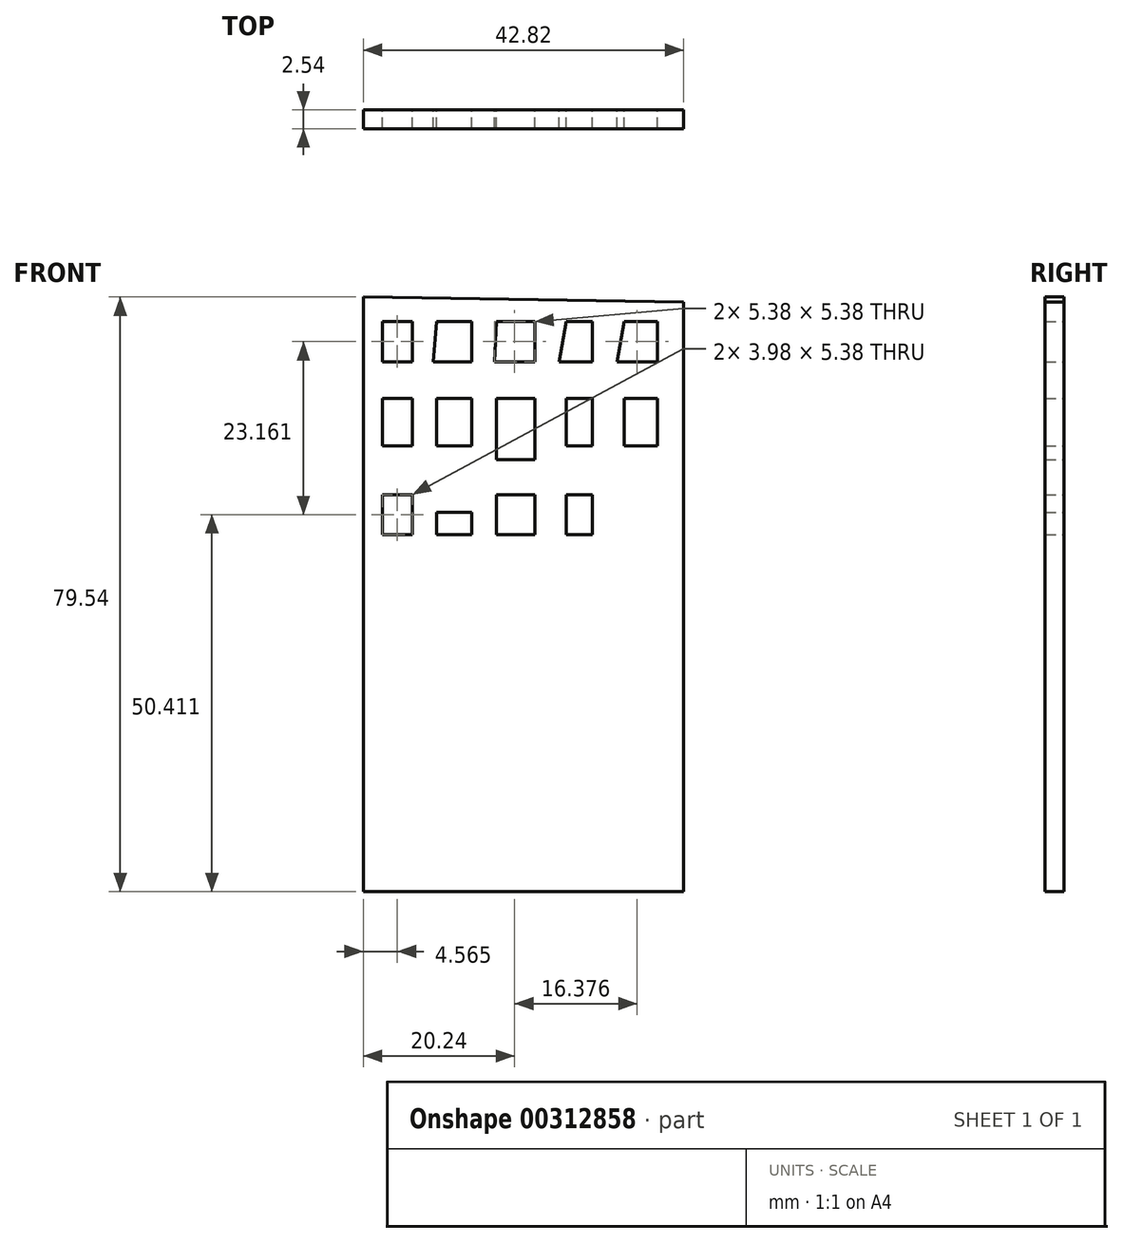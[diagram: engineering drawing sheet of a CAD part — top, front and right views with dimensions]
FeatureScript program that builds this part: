
annotation { "Feature Type Name" : "Feature", "Feature Type Description" : "" }
export const myFeature = defineFeature(function(context is Context, id is Id, definition is map)
    precondition{}
    {
        {
            var Q0;
            Q0=qCreatedBy(makeId("Front.planeOp"),FACE);
            var sketch = newSketch(context, id + "F0", { "sketchPlane" : qUnion([Q0])});
            skLineSegment(sketch, "E0", {"start": v(19.89, 35.33) * mm, "end": v(19.89, -43.51) * mm});
            skLineSegment(sketch, "E1", {"start": v(19.89, -43.51) * mm, "end": v(-22.93, -43.51) * mm});
            skLineSegment(sketch, "E2", {"start": v(-22.93, -43.51) * mm, "end": v(-22.93, 36.03) * mm});
            skLineSegment(sketch, "E3", {"start": v(-22.93, 36.03) * mm, "end": v(19.89, 35.33) * mm});
            skLineSegment(sketch, "E4", {"start": v(-22.93, -31.35) * mm, "end": v(19.89, -32.05) * mm});
            skCircle(sketch, "E5", {"center": v(0, -37.67) * mm, "radius": 4 * mm});
            skLineSegment(sketch, "E6", {"start": v(-20.35, 32.75) * mm, "end": v(-20.35, 27.37) * mm});
            skLineSegment(sketch, "E7", {"start": v(-20.35, 27.37) * mm, "end": v(-16.38, 27.37) * mm});
            skLineSegment(sketch, "E8", {"start": v(-16.38, 27.37) * mm, "end": v(-16.38, 32.75) * mm});
            skLineSegment(sketch, "E9", {"start": v(-16.38, 32.75) * mm, "end": v(-20.35, 32.75) * mm});
            skLineSegment(sketch, "E10", {"start": v(-13.1, 32.75) * mm, "end": v(-8.42, 32.75) * mm});
            skPoint(sketch, "E10.startSnap0", {"position": v(-18.36, 32.75) * mm});
            skPoint(sketch, "E10.endSnap0", {"position": v(-18.36, 32.75) * mm});
            skLineSegment(sketch, "E11", {"start": v(-8.42, 32.75) * mm, "end": v(-8.42, 27.37) * mm});
            skLineSegment(sketch, "E12", {"start": v(-8.42, 27.37) * mm, "end": v(-13.57, 27.37) * mm});
            skLineSegment(sketch, "E13", {"start": v(-13.57, 27.37) * mm, "end": v(-13.1, 32.75) * mm});
            skLineSegment(sketch, "E14", {"start": v(-5.15, 32.75) * mm, "end": v(0, 32.75) * mm});
            skPoint(sketch, "E14.startSnap0", {"position": v(-10.76, 32.75) * mm});
            skLineSegment(sketch, "E15", {"start": v(0, 32.75) * mm, "end": v(0, 27.37) * mm});
            skLineSegment(sketch, "E16", {"start": v(0, 27.37) * mm, "end": v(-5.38, 27.37) * mm});
            skLineSegment(sketch, "E17", {"start": v(-5.38, 27.37) * mm, "end": v(-5.15, 32.75) * mm});
            skLineSegment(sketch, "E18", {"start": v(4.21, 32.75) * mm, "end": v(7.72, 32.75) * mm});
            skLineSegment(sketch, "E19", {"start": v(7.72, 32.75) * mm, "end": v(7.72, 27.37) * mm});
            skLineSegment(sketch, "E20", {"start": v(7.72, 27.37) * mm, "end": v(3.28, 27.37) * mm});
            skLineSegment(sketch, "E21", {"start": v(3.28, 27.37) * mm, "end": v(4.21, 32.75) * mm});
            skLineSegment(sketch, "E22", {"start": v(11.93, 32.75) * mm, "end": v(16.38, 32.75) * mm});
            skLineSegment(sketch, "E23", {"start": v(16.38, 32.75) * mm, "end": v(16.38, 27.37) * mm});
            skLineSegment(sketch, "E24", {"start": v(16.38, 27.37) * mm, "end": v(11, 27.37) * mm});
            skLineSegment(sketch, "E25", {"start": v(11, 27.37) * mm, "end": v(11.93, 32.75) * mm});
            skLineSegment(sketch, "E26", {"start": v(-16.38, 22.46) * mm, "end": v(-20.35, 22.46) * mm});
            skLineSegment(sketch, "E27", {"start": v(-20.35, 22.46) * mm, "end": v(-20.35, 16.14) * mm});
            skLineSegment(sketch, "E28", {"start": v(-20.35, 16.14) * mm, "end": v(-16.38, 16.14) * mm});
            skLineSegment(sketch, "E29", {"start": v(-16.38, 16.14) * mm, "end": v(-16.38, 22.46) * mm});
            skLineSegment(sketch, "E30", {"start": v(-16.38, 9.6) * mm, "end": v(-20.35, 9.6) * mm});
            skLineSegment(sketch, "E31", {"start": v(-20.35, 9.6) * mm, "end": v(-20.35, 4.21) * mm});
            skLineSegment(sketch, "E32", {"start": v(-20.35, 4.21) * mm, "end": v(-16.38, 4.21) * mm});
            skLineSegment(sketch, "E33", {"start": v(-16.38, 4.21) * mm, "end": v(-16.38, 9.6) * mm});
            skLineSegment(sketch, "E34", {"start": v(-8.42, 22.46) * mm, "end": v(-13.1, 22.46) * mm});
            skLineSegment(sketch, "E35", {"start": v(-13.1, 22.46) * mm, "end": v(-13.1, 16.14) * mm});
            skLineSegment(sketch, "E36", {"start": v(-13.1, 16.14) * mm, "end": v(-8.42, 16.14) * mm});
            skLineSegment(sketch, "E37", {"start": v(-8.42, 16.14) * mm, "end": v(-8.42, 22.46) * mm});
            skLineSegment(sketch, "E38", {"start": v(0, 22.46) * mm, "end": v(-5.15, 22.46) * mm});
            skLineSegment(sketch, "E39", {"start": v(-5.15, 22.46) * mm, "end": v(-5.15, 14.27) * mm});
            skLineSegment(sketch, "E40", {"start": v(-5.15, 14.27) * mm, "end": v(0, 14.27) * mm});
            skLineSegment(sketch, "E41", {"start": v(0, 14.27) * mm, "end": v(0, 22.46) * mm});
            skLineSegment(sketch, "E42", {"start": v(7.72, 22.46) * mm, "end": v(4.21, 22.46) * mm});
            skLineSegment(sketch, "E43", {"start": v(4.21, 22.46) * mm, "end": v(4.21, 16.14) * mm});
            skLineSegment(sketch, "E44", {"start": v(4.21, 16.14) * mm, "end": v(7.72, 16.14) * mm});
            skLineSegment(sketch, "E45", {"start": v(7.72, 16.14) * mm, "end": v(7.72, 22.46) * mm});
            skLineSegment(sketch, "E46", {"start": v(16.38, 22.46) * mm, "end": v(11.93, 22.46) * mm});
            skLineSegment(sketch, "E47", {"start": v(11.93, 22.46) * mm, "end": v(11.93, 16.14) * mm});
            skLineSegment(sketch, "E48", {"start": v(11.93, 16.14) * mm, "end": v(16.38, 16.14) * mm});
            skLineSegment(sketch, "E49", {"start": v(16.38, 16.14) * mm, "end": v(16.38, 22.46) * mm});
            skLineSegment(sketch, "E50", {"start": v(-8.42, 7.25) * mm, "end": v(-13.1, 7.25) * mm});
            skLineSegment(sketch, "E51", {"start": v(-13.1, 7.25) * mm, "end": v(-13.1, 4.21) * mm});
            skLineSegment(sketch, "E52", {"start": v(-13.1, 4.21) * mm, "end": v(-8.42, 4.21) * mm});
            skLineSegment(sketch, "E53", {"start": v(-8.42, 4.21) * mm, "end": v(-8.42, 7.25) * mm});
            skLineSegment(sketch, "E54", {"start": v(0, 9.6) * mm, "end": v(-5.15, 9.6) * mm});
            skLineSegment(sketch, "E55", {"start": v(-5.15, 9.6) * mm, "end": v(-5.15, 4.21) * mm});
            skLineSegment(sketch, "E56", {"start": v(-5.15, 4.21) * mm, "end": v(0, 4.21) * mm});
            skLineSegment(sketch, "E57", {"start": v(0, 4.21) * mm, "end": v(0, 9.6) * mm});
            skLineSegment(sketch, "E58", {"start": v(7.72, 9.6) * mm, "end": v(4.21, 9.6) * mm});
            skLineSegment(sketch, "E59", {"start": v(4.21, 9.6) * mm, "end": v(4.21, 4.21) * mm});
            skLineSegment(sketch, "E60", {"start": v(4.21, 4.21) * mm, "end": v(7.72, 4.21) * mm});
            skLineSegment(sketch, "E61", {"start": v(7.72, 4.21) * mm, "end": v(7.72, 9.6) * mm});
            skLineSegment(sketch, "E62", {"start": v(16.38, 9.6) * mm, "end": v(11.93, 9.6) * mm});
            skLineSegment(sketch, "E63", {"start": v(11.93, 9.6) * mm, "end": v(11.93, 4.21) * mm});
            skLineSegment(sketch, "E64", {"start": v(11.93, 4.21) * mm, "end": v(16.38, 4.21) * mm});
            skLineSegment(sketch, "E65", {"start": v(16.38, 4.21) * mm, "end": v(17.78, 9.6) * mm});
            skSolve(sketch);
        }
        {
            var Q0;
            {var subQ0=sQuery(id+"F0.wireOp",EDGE,"E3");Q0=makeQuery(id+"F0.imprint","IMPRINT",FACE,{"disambiguationData":[TD([[makeQuery(id+"F0.imprint","IMPRINT",EDGE,{"derivedFrom":subQ0}),-1.0]])]});}
            var Q1;
            {var subQ1=sQuery(id+"F0.wireOp",EDGE,"E1");Q1=makeQuery(id+"F0.imprint","IMPRINT",FACE,{"disambiguationData":[TD([[makeQuery(id+"F0.imprint","IMPRINT",EDGE,{"derivedFrom":subQ1}),-1.0]])]});}
            var Q2;
            Q2=makeQuery(id+"F0.imprint","IMPRINT",FACE,{"disambiguationData":[TD([[makeQuery(id+"F0.imprint","IMPRINT",EDGE,{"derivedFrom":sQuery(id+"F0.wireOp",EDGE,"E5")}),1.0]])]});
            extrude(context, id + "F1", {"entities" : qUnion([Q0, Q1, Q2]), "depth" : 2.54 * mm});
        }
    });
